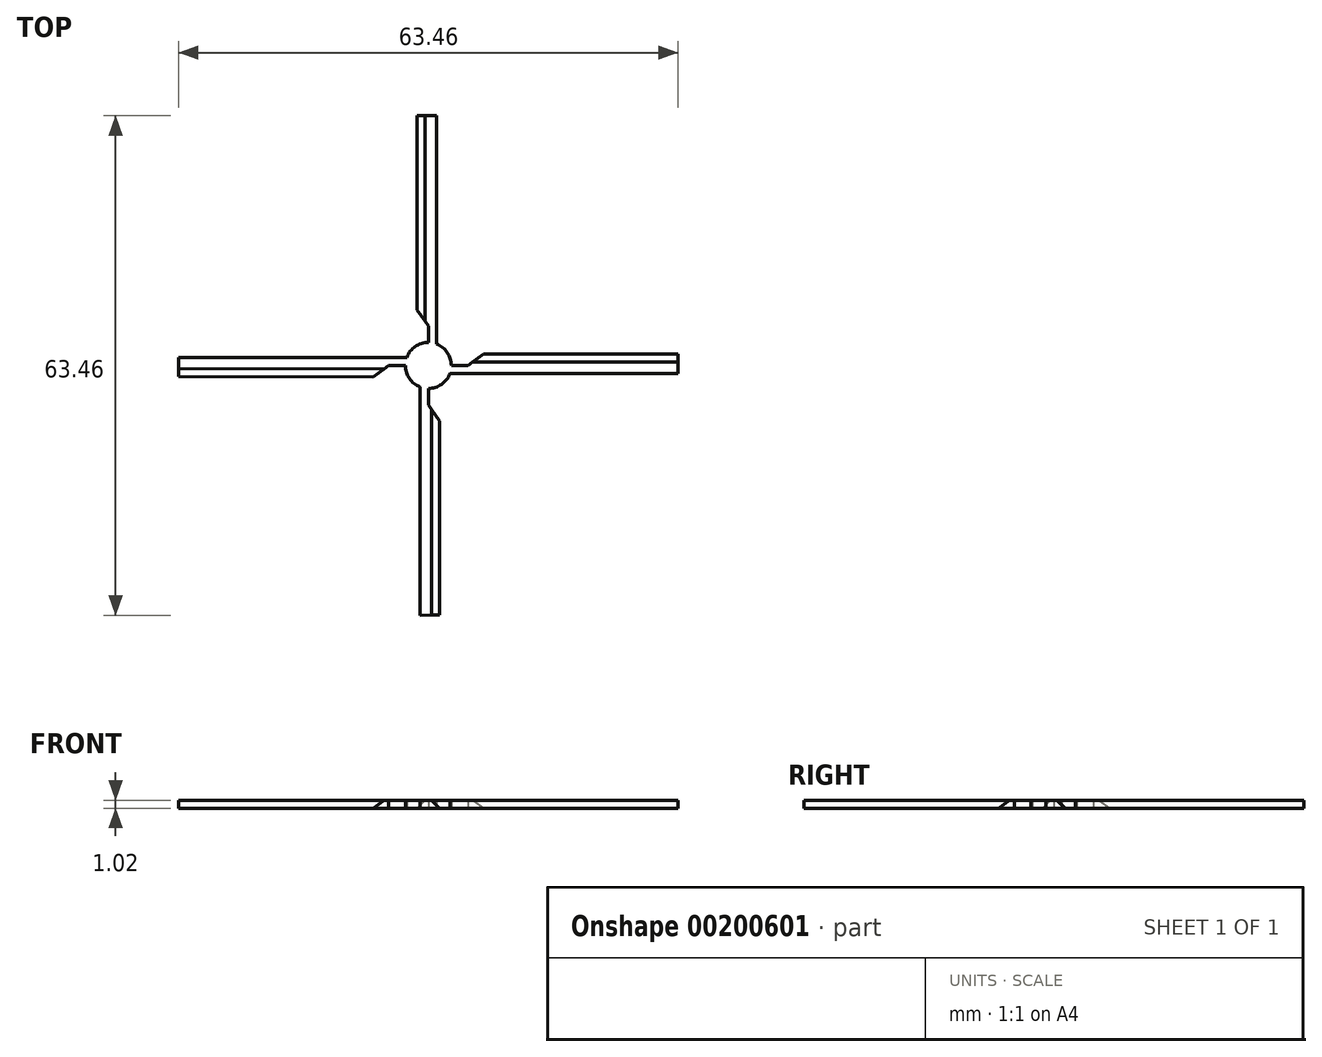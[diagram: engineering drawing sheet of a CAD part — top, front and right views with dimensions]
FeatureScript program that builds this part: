
annotation { "Feature Type Name" : "Feature", "Feature Type Description" : "" }
export const myFeature = defineFeature(function(context is Context, id is Id, definition is map)
    precondition{}
    {
        {
            var Q0;
            Q0=qCreatedBy(makeId("Top.planeOp"),FACE);
            var sketch = newSketch(context, id + "F0", { "sketchPlane" : qUnion([Q0])});
            skCircle(sketch, "E0", {"center": v(0, 0) * mm, "radius": 31.75 * mm, "construction": true});
            skCircle(sketch, "E1", {"center": v(0, 0) * mm, "radius": 2.92 * mm});
            skLineSegment(sketch, "E2", {"start": v(-1.42, 31.72) * mm, "end": v(1.04, 31.73) * mm});
            skLineSegment(sketch, "E3", {"start": v(1.04, 31.73) * mm, "end": v(1.04, 1.75) * mm});
            skLineSegment(sketch, "E4", {"start": v(1.04, 1.75) * mm, "end": v(0, 2.92) * mm});
            skLineSegment(sketch, "E5", {"start": v(0, 2.92) * mm, "end": v(0, 5.02) * mm});
            skLineSegment(sketch, "E6", {"start": v(0, 5.02) * mm, "end": v(-1.44, 7.04) * mm});
            skLineSegment(sketch, "E7", {"start": v(-1.44, 7.04) * mm, "end": v(-1.42, 31.72) * mm});
            skLineSegment(sketch, "E8.1.0", {"start": v(-31.72, -1.42) * mm, "end": v(-31.73, 1.04) * mm});
            skLineSegment(sketch, "E8.1.1", {"start": v(-31.73, 1.04) * mm, "end": v(-1.75, 1.04) * mm});
            skLineSegment(sketch, "E8.1.2", {"start": v(-1.75, 1.04) * mm, "end": v(-2.92, 0) * mm});
            skLineSegment(sketch, "E8.1.3", {"start": v(-2.92, 0) * mm, "end": v(-5.02, 0) * mm});
            skLineSegment(sketch, "E8.1.4", {"start": v(-5.02, 0) * mm, "end": v(-7.04, -1.44) * mm});
            skLineSegment(sketch, "E8.1.5", {"start": v(-7.04, -1.44) * mm, "end": v(-31.72, -1.42) * mm});
            skLineSegment(sketch, "E8.2.0", {"start": v(1.42, -31.72) * mm, "end": v(-1.04, -31.73) * mm});
            skLineSegment(sketch, "E8.2.1", {"start": v(-1.04, -31.73) * mm, "end": v(-1.04, -1.75) * mm});
            skLineSegment(sketch, "E8.2.2", {"start": v(-1.04, -1.75) * mm, "end": v(0, -2.92) * mm});
            skLineSegment(sketch, "E8.2.3", {"start": v(0, -2.92) * mm, "end": v(0, -5.02) * mm});
            skLineSegment(sketch, "E8.2.4", {"start": v(0, -5.02) * mm, "end": v(1.44, -7.04) * mm});
            skLineSegment(sketch, "E8.2.5", {"start": v(1.44, -7.04) * mm, "end": v(1.42, -31.72) * mm});
            skLineSegment(sketch, "E9.1.3.0", {"start": v(31.72, 1.42) * mm, "end": v(31.73, -1.04) * mm});
            skLineSegment(sketch, "E9.3.3.0", {"start": v(31.73, -1.04) * mm, "end": v(1.75, -1.04) * mm});
            skLineSegment(sketch, "E9.6.3.0", {"start": v(1.75, -1.04) * mm, "end": v(2.92, 0) * mm});
            skLineSegment(sketch, "E9.9.3.0", {"start": v(2.92, 0) * mm, "end": v(5.02, 0) * mm});
            skLineSegment(sketch, "E9.12.3.0", {"start": v(5.02, 0) * mm, "end": v(7.04, 1.44) * mm});
            skLineSegment(sketch, "E9.15.3.0", {"start": v(7.04, 1.44) * mm, "end": v(31.72, 1.42) * mm});
            skSolve(sketch);
        }
        {
            var Q0;
            {var subQ2=sQuery(id+"F0.wireOp",EDGE,"E2");Q0=makeQuery(id+"F0.imprint","IMPRINT",FACE,{"disambiguationData":[TD([[makeQuery(id+"F0.imprint","IMPRINT",EDGE,{"derivedFrom":subQ2}),-1.0]])]});}
            var Q1;
            {var subQ0=sQuery(id+"F0.wireOp",EDGE,"E4");Q1=makeQuery(id+"F0.imprint","IMPRINT",FACE,{"disambiguationData":[TD([[makeQuery(id+"F0.imprint","IMPRINT",EDGE,{"derivedFrom":subQ0}),-1.0]])]});}
            var Q2;
            {var subQ3=sQuery(id+"F0.wireOp",EDGE,"E4");Q2=makeQuery(id+"F0.imprint","IMPRINT",FACE,{"disambiguationData":[TD([[makeQuery(id+"F0.imprint","IMPRINT",EDGE,{"derivedFrom":subQ3}),1.0]])]});}
            var Q3;
            {var subQ0=sQuery(id+"F0.wireOp",EDGE,"E8.1.2");Q3=makeQuery(id+"F0.imprint","IMPRINT",FACE,{"disambiguationData":[TD([[makeQuery(id+"F0.imprint","IMPRINT",EDGE,{"derivedFrom":subQ0}),-1.0]])]});}
            var Q4;
            {var subQ0=sQuery(id+"F0.wireOp",EDGE,"E9.6.3.0");Q4=makeQuery(id+"F0.imprint","IMPRINT",FACE,{"disambiguationData":[TD([[makeQuery(id+"F0.imprint","IMPRINT",EDGE,{"derivedFrom":subQ0}),-1.0]])]});}
            var Q5;
            {var subQ1=sQuery(id+"F0.wireOp",EDGE,"E9.1.3.0");Q5=makeQuery(id+"F0.imprint","IMPRINT",FACE,{"disambiguationData":[TD([[makeQuery(id+"F0.imprint","IMPRINT",EDGE,{"derivedFrom":subQ1}),-1.0]])]});}
            var Q6;
            {var subQ0=sQuery(id+"F0.wireOp",EDGE,"E8.2.2");Q6=makeQuery(id+"F0.imprint","IMPRINT",FACE,{"disambiguationData":[TD([[makeQuery(id+"F0.imprint","IMPRINT",EDGE,{"derivedFrom":subQ0}),-1.0]])]});}
            var Q7;
            {var subQ2=sQuery(id+"F0.wireOp",EDGE,"E8.2.0");Q7=makeQuery(id+"F0.imprint","IMPRINT",FACE,{"disambiguationData":[TD([[makeQuery(id+"F0.imprint","IMPRINT",EDGE,{"derivedFrom":subQ2}),-1.0]])]});}
            var Q8;
            {var subQ1=sQuery(id+"F0.wireOp",EDGE,"E8.1.0");Q8=makeQuery(id+"F0.imprint","IMPRINT",FACE,{"disambiguationData":[TD([[makeQuery(id+"F0.imprint","IMPRINT",EDGE,{"derivedFrom":subQ1}),-1.0]])]});}
            extrude(context, id + "F1", {"entities" : qUnion([Q0, Q1, Q2, Q3, Q4, Q5, Q6, Q7, Q8]), "depth" : 1.02 * mm});
        }
        {
            var Q0;
            Q0=makeQuery(id+"F1.opExtrude","CAP_EDGE",EDGE,{"disambiguationData":[OSD([sQuery(id+"F0.wireOp",EDGE,"E8.1.5")])],"isStart":false});
            var Q1;
            Q1=makeQuery(id+"F1.opExtrude","CAP_EDGE",EDGE,{"disambiguationData":[OSD([sQuery(id+"F0.wireOp",EDGE,"E8.2.5")])],"isStart":false});
            var Q2;
            Q2=makeQuery(id+"F1.opExtrude","CAP_EDGE",EDGE,{"disambiguationData":[OSD([sQuery(id+"F0.wireOp",EDGE,"E9.15.3.0")])],"isStart":false});
            var Q3;
            Q3=makeQuery(id+"F1.opExtrude","CAP_EDGE",EDGE,{"disambiguationData":[OSD([sQuery(id+"F0.wireOp",EDGE,"E7")])],"isStart":false});
            chamfer(context, id + "F2", {"entities" : qUnion([Q0, Q1, Q2, Q3]), "width" : 1.02 * mm, "tangentPropagation" : true});
        }
    });
